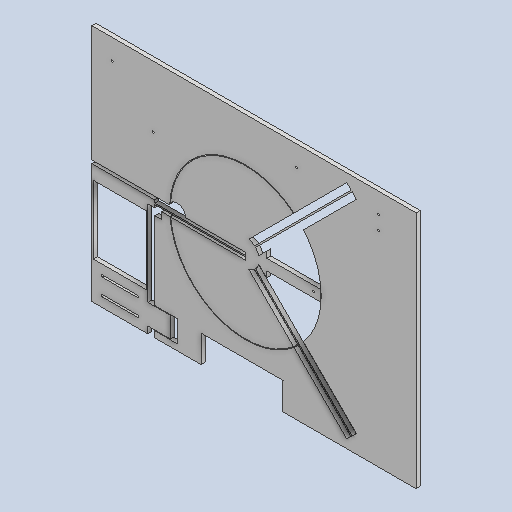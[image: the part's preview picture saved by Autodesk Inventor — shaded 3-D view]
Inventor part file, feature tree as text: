
AUTODESK INVENTOR PART (.ipt)
format: ipt  version: 2023 (Build 270158000, 158)  size: 401,920 bytes
history: native  units: mm
features: extrude x8, sketch x8, reference x5, other x3, projected_geometry x1
ambient origin geometry x8: Origin, YZ Plane, XZ Plane, XY Plane, X Axis, Y Axis, Z Axis, Center Point
bodies: Solid1 (feature_tree)
feature tree (25):
  extrude  "Extrusion1"  Depth=400.0mm
  extrude  "Extrusion2"  TaperAngle=0.0deg  [1 undecoded]
  extrude  "Extrusion3"  Depth=175.0mm
  extrude  "Extrusion4"  Depth=40.0mm
  extrude  "Extrusion5"  Depth=10.0mm
  extrude  "Extrusion6"  Depth=10.0mm
  extrude  "Extrusion7"  Depth=1.0mm
  extrude  "Extrusion8"  Depth=1.0mm
  sketch  "Sketch1"  dims[d0=350.0mm d1=400.0mm]
  sketch  "Sketch2"  dims[d2=6.0mm d3=0.0mm]
  reference  "Reference1"
  sketch  "Sketch3"  dims[d4=175.0mm d5=175.0mm]
  sketch  "Sketch4"  dims[d6=220.0mm d7=40.0mm]
  sketch  "Sketch5"  dims[d8=10.0mm d9=10.0mm]
  projected_geometry  "Projected Loop1"
  sketch  "Sketch6"  dims[d10=10.0mm d11=10.0mm]
  sketch  "Sketch7"  dims[d12=1.0mm d13=1.0mm]
  sketch  "Sketch8"  dims[d14=1.0mm d15=1.0mm d16=200.0mm d17=200.0mm d18=222.0mm d19=100.0mm d20=2.25mm d21=2.25mm d22=10.0mm d24=20.0mm d25=0.0mm d26=6.0mm d27=4.0mm d28=4.0mm d29=20.0mm d30=0.0mm d31=1.0mm d32=1.0mm d33=10.0mm d34=30.0mm d35=10.0mm d36=100.0mm d37=0.0mm d38=3.0mm d39=6.0mm d40=0.0mm d41=25.0mm d42=40.0mm d43=120.0mm d44=120.0mm d45=6.0mm d46=0.0mm d47=3.0mm d48=30.0mm d49=30.0mm d50=90.0mm d51=90.0mm d52=3.0mm d53=3.0mm d54=100.0mm d55=30.0mm d56=6.0mm d57=0.0mm d61=8.0mm d62=8.0mm d63=10.0mm d64=0.0mm d65=15.0mm d66=15.0mm d67=15.0mm d68=15.0mm d69=15.0mm d70=15.0mm d71=15.0mm d72=15.0mm d73=3.0mm d74=3.0mm d75=3.0mm d76=3.0mm d77=52.128569mm d78=10.0mm d79=0.0mm d80=25.0mm d81=475.0mm d82=6.0mm d83=0.0mm d84=3.0mm d85=3.0mm d86=15.0mm d87=15.0mm d88=6.0mm d89=0.0mm]
  reference  "Reference2"
  reference  "Reference3"
  reference  "Reference4"
  reference  "Reference5"
  other  "<userpath>\OneDrive\ClawdDrive\Objet3D\IminaProbe\RoueMDF\Assembly1.iam"
  other  "Assembly1.iam"
  other  "Inverter:1"
note: 1 required parameter value undecoded (feature->parameter linkage not recoverable at this tier; creation-order binding heuristic only, values carry confidence <= 0.55)
